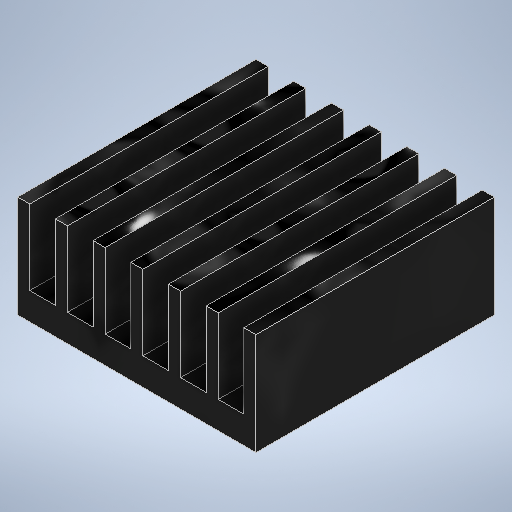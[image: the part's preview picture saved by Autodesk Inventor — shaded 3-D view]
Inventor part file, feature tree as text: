
AUTODESK INVENTOR PART (.ipt)
format: ipt  version: 2025 (Build 290162000, 162)  size: 279,552 bytes
history: native  units: mm
features: extrude x2, sketch x2, projected_geometry x1
ambient origin geometry x8: Origin, YZ Plane, XZ Plane, XY Plane, X Axis, Y Axis, Z Axis, Center Point
bodies: Solid1 (feature_tree)
feature tree (5):
  extrude  "Extrusion1"  Depth=14.0mm
  extrude  "Extrusion2"  Depth=6.0mm
  sketch  "Sketch1"  dims[d0=14.0mm d1=14.0mm]
  sketch  "Sketch2"  dims[d2=6.0mm d3=0.0mm d4=6.0mm d5=1.6mm d6=1.5mm d8=1.5mm d9=1.5mm d10=1.5mm d11=1.5mm d12=1.5mm d13=0.0mm d14=0.0mm]
  projected_geometry  "Projected Loop1"
